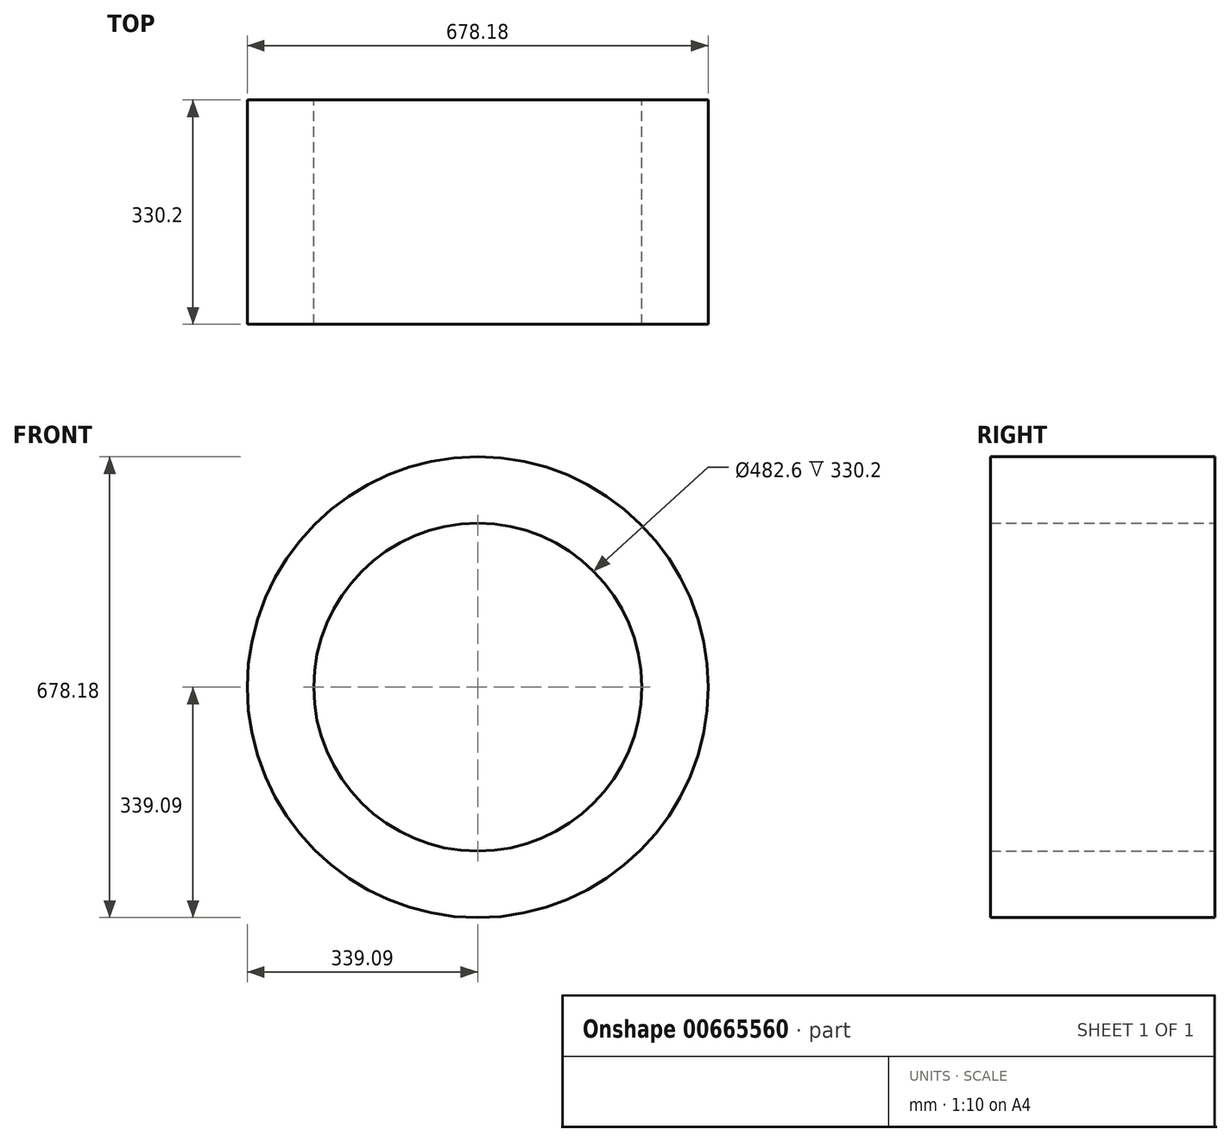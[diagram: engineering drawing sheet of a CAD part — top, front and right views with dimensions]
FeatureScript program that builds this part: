
annotation { "Feature Type Name" : "Feature", "Feature Type Description" : "" }
export const myFeature = defineFeature(function(context is Context, id is Id, definition is map)
    precondition{}
    {
        {
            var Q0;
            Q0=qCreatedBy(makeId("Front.planeOp"),FACE);
            var sketch = newSketch(context, id + "F0", { "sketchPlane" : qUnion([Q0])});
            skCircle(sketch, "E0", {"center": v(0, 0) * mm, "radius": 241.3 * mm});
            skCircle(sketch, "E1", {"center": v(0, 0) * mm, "radius": 339.09 * mm});
            skSolve(sketch);
        }
        {
            var Q0;
            Q0=makeQuery(id+"F0.imprint","IMPRINT",FACE,{"disambiguationData":[TD([[makeQuery(id+"F0.imprint","IMPRINT",EDGE,{"derivedFrom":sQuery(id+"F0.wireOp",EDGE,"E0")}),-1.0]])]});
            extrude(context, id + "F1", {"entities" : qUnion([Q0]), "depth" : 330.2 * mm, "offsetDistance" : 25.4 * mm});
        }
    });
